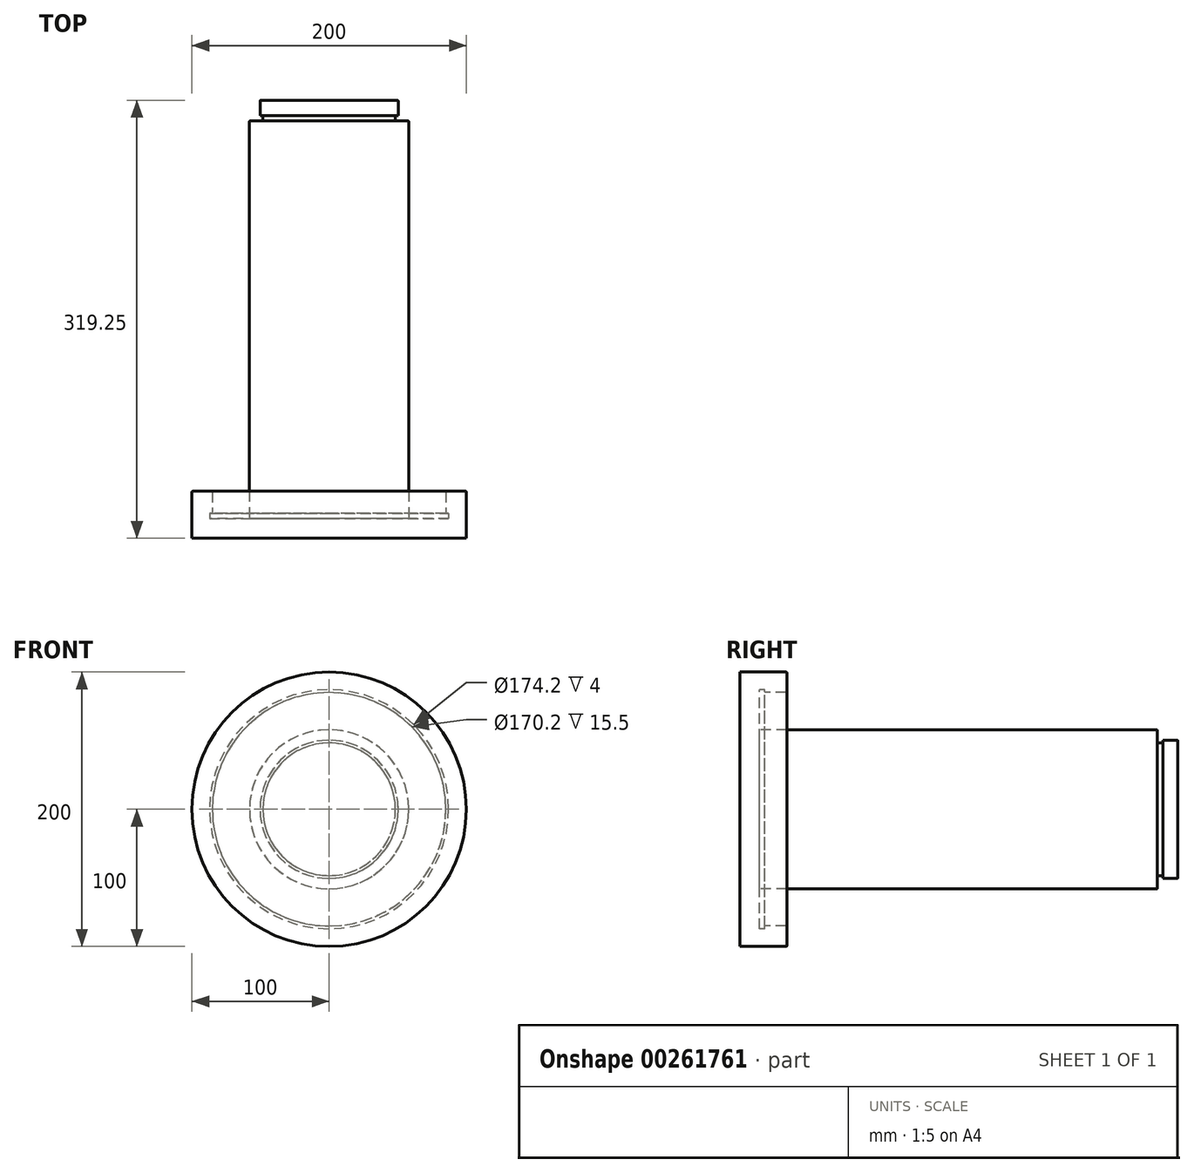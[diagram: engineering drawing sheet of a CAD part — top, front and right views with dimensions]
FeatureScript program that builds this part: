
annotation { "Feature Type Name" : "Feature", "Feature Type Description" : "" }
export const myFeature = defineFeature(function(context is Context, id is Id, definition is map)
    precondition{}
    {
        {
            var Q0;
            Q0=qCreatedBy(makeId("Right.planeOp"),FACE);
            var sketch = newSketch(context, id + "F0", { "sketchPlane" : qUnion([Q0])});
            skLineSegment(sketch, "E0", {"start": v(0, 0) * mm, "end": v(319.25, 0) * mm});
            skLineSegment(sketch, "E1", {"start": v(0, 0) * mm, "end": v(0, 100) * mm});
            skLineSegment(sketch, "E2", {"start": v(0, 100) * mm, "end": v(34.25, 100) * mm});
            skLineSegment(sketch, "E3", {"start": v(34.25, 100) * mm, "end": v(34.25, 85.1) * mm});
            skLineSegment(sketch, "E4", {"start": v(34.25, 85.1) * mm, "end": v(18.25, 85.1) * mm});
            skLineSegment(sketch, "E5", {"start": v(18.25, 85.1) * mm, "end": v(18.25, 87.1) * mm});
            skLineSegment(sketch, "E6", {"start": v(18.25, 87.1) * mm, "end": v(14.25, 87.1) * mm});
            skLineSegment(sketch, "E7", {"start": v(14.25, 87.1) * mm, "end": v(14.25, 58) * mm});
            skLineSegment(sketch, "E8", {"start": v(14.25, 58) * mm, "end": v(304.25, 58) * mm});
            skLineSegment(sketch, "E9", {"start": v(304.25, 58) * mm, "end": v(304.25, 48.35) * mm});
            skLineSegment(sketch, "E10", {"start": v(304.25, 48.35) * mm, "end": v(308.25, 48.35) * mm});
            skLineSegment(sketch, "E11", {"start": v(308.25, 48.35) * mm, "end": v(308.25, 50.35) * mm});
            skLineSegment(sketch, "E12", {"start": v(308.25, 50.35) * mm, "end": v(319.25, 50.35) * mm});
            skLineSegment(sketch, "E13", {"start": v(319.25, 50.35) * mm, "end": v(319.25, 0) * mm});
            skSolve(sketch);
        }
        {
            var Q0;
            Q0 = qSketchRegion(id + "F0", true);
            var Q1;
            Q1=sQuery(id+"F0.wireOp",EDGE,"E0");
            revolve(context, id + "F1", {"entities" : qUnion([Q0]), "axis" : qUnion([Q1]), "revolveType" : RevolveType.ONE_DIRECTION, "angle" : 360 * degree});
        }
        {
            var Q0;
            Q0=makeQuery(id+"F1.opRevolve","SWEPT_FACE",FACE,{"disambiguationData":[OSD([sQuery(id+"F0.wireOp",EDGE,"E13")])]});
            var Q1;
            Q1=makeQuery(id+"F1.opRevolve","SWEPT_FACE",FACE,{"disambiguationData":[OSD([sQuery(id+"F0.wireOp",EDGE,"E9")])]});
            var Q2;
            Q2=makeQuery(id+"F1.opRevolve","SWEPT_FACE",FACE,{"disambiguationData":[OSD([sQuery(id+"F0.wireOp",EDGE,"E3")])]});
            fillet(context, id + "F2", {"entities" : qUnion([Q0, Q1, Q2]), "radius" : 0.5 * mm, "tangentPropagation" : true, "allowEdgeOverflow" : false});
        }
    });
